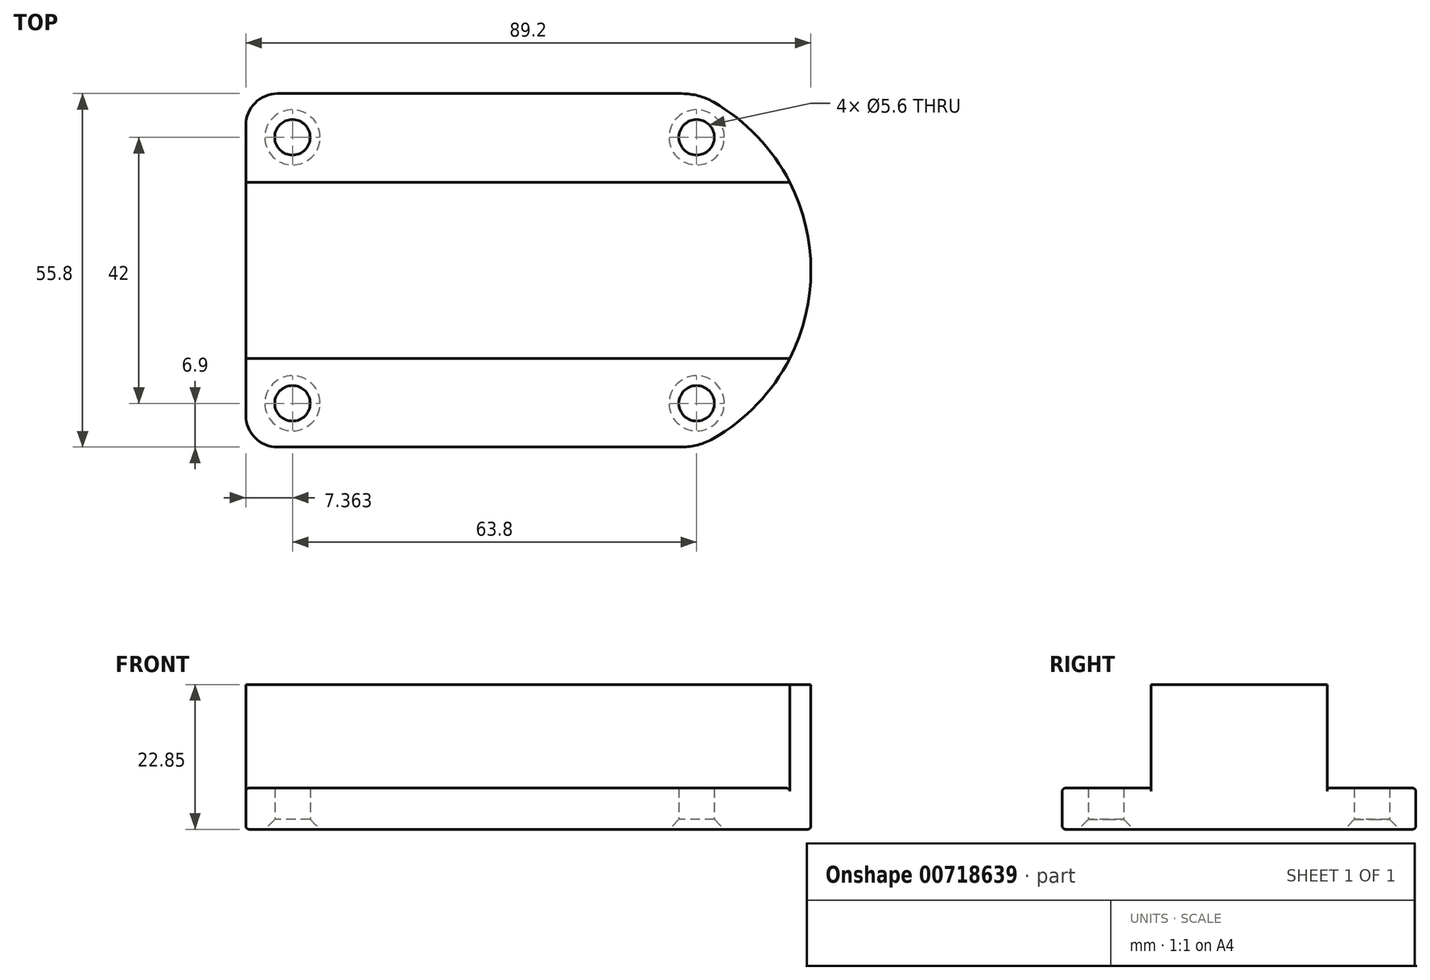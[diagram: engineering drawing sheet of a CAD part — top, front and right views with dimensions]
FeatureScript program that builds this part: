
annotation { "Feature Type Name" : "Feature", "Feature Type Description" : "" }
export const myFeature = defineFeature(function(context is Context, id is Id, definition is map)
    precondition{}
    {
        {
            var Q0;
            Q0=qCreatedBy(makeId("Top.planeOp"),FACE);
            var sketch = newSketch(context, id + "F0", { "sketchPlane" : qUnion([Q0])});
            skLineSegment(sketch, "E0.bottom", {"start": v(-38.88, -28.9) * mm, "end": v(-38.88, 16.9) * mm});
            skLineSegment(sketch, "E0.left", {"start": v(-33.88, -33.9) * mm, "end": v(29.94, -33.9) * mm});
            skLineSegment(sketch, "E0.right", {"start": v(-33.88, 21.9) * mm, "end": v(29.94, 21.9) * mm});
            skArc(sketch, "E1", {"start": v(34.9, -32.58) * mm, "mid": v(50.32, -6) * mm, "end": v(34.9, 20.58) * mm});
            skPoint(sketch, "E2.visualSharp", {"position": v(32.32, 21.9) * mm});
            skArc(sketch, "E2.filletArc", {"start": v(34.9, 20.58) * mm, "mid": v(32.51, 21.56) * mm, "end": v(29.94, 21.9) * mm});
            skPoint(sketch, "E3.visualSharp", {"position": v(32.32, -33.9) * mm});
            skArc(sketch, "E3.filletArc", {"start": v(29.94, -33.9) * mm, "mid": v(32.51, -33.56) * mm, "end": v(34.9, -32.58) * mm});
            skCircle(sketch, "E4", {"center": v(-31.52, 15) * mm, "radius": 2.8 * mm});
            skCircle(sketch, "E5", {"center": v(-31.52, -27) * mm, "radius": 2.8 * mm});
            skCircle(sketch, "E6", {"center": v(32.28, -27) * mm, "radius": 2.8 * mm});
            skCircle(sketch, "E7", {"center": v(32.28, 15) * mm, "radius": 2.8 * mm});
            skPoint(sketch, "E8.visualSharp", {"position": v(-38.88, 21.9) * mm});
            skArc(sketch, "E8.filletArc", {"start": v(-33.88, 21.9) * mm, "mid": v(-37.41, 20.44) * mm, "end": v(-38.88, 16.9) * mm});
            skPoint(sketch, "E9.visualSharp", {"position": v(-38.88, -33.9) * mm});
            skArc(sketch, "E9.filletArc", {"start": v(-38.88, -28.9) * mm, "mid": v(-37.41, -32.44) * mm, "end": v(-33.88, -33.9) * mm});
            skSolve(sketch);
        }
        {
            var Q0;
            Q0 = qSketchRegion(id + "F0", true);
            extrude(context, id + "F1", {"entities" : qUnion([Q0]), "depth" : 6.5 * mm, "offsetDistance" : 25 * mm});
        }
        {
            var Q0;
            Q0=makeQuery(id+"F1.opExtrude","CAP_FACE",FACE,{"disambiguationData":[OSD([sQuery(id+"F0.wireOp",EDGE,"E0.bottom"),sQuery(id+"F0.wireOp",EDGE,"E0.left"),sQuery(id+"F0.wireOp",EDGE,"E0.right"),sQuery(id+"F0.wireOp",EDGE,"E1"),sQuery(id+"F0.wireOp",EDGE,"E2.filletArc"),sQuery(id+"F0.wireOp",EDGE,"E3.filletArc"),sQuery(id+"F0.wireOp",EDGE,"E4"),sQuery(id+"F0.wireOp",EDGE,"E5"),sQuery(id+"F0.wireOp",EDGE,"E6"),sQuery(id+"F0.wireOp",EDGE,"E7")])],"isStart":false});
            var sketch = newSketch(context, id + "F2", { "sketchPlane" : qUnion([Q0])});
            skLineSegment(sketch, "E10", {"start": v(-38.88, -6) * mm, "end": v(-38.88, 7.9) * mm});
            skLineSegment(sketch, "E11", {"start": v(-38.88, -6) * mm, "end": v(-38.88, -19.9) * mm});
            skLineSegment(sketch, "E12.bottom", {"start": v(-38.88, 7.9) * mm, "end": v(46.99, 7.9) * mm});
            skLineSegment(sketch, "E12.top", {"start": v(-38.88, -19.9) * mm, "end": v(46.99, -19.9) * mm});
            skLineSegment(sketch, "E12.left", {"start": v(-38.88, 7.9) * mm, "end": v(-38.88, -19.9) * mm});
            skArc(sketch, "E13", {"start": v(46.99, -19.9) * mm, "mid": v(50.32, -6) * mm, "end": v(46.99, 7.9) * mm});
            skSolve(sketch);
        }
        {
            var Q0;
            Q0 = qSketchRegion(id + "F2", true);
            extrude(context, id + "F3", {"entities" : qUnion([Q0]), "operationType" : NewBodyOperationType.ADD, "depth" : 16.35 * mm, "offsetDistance" : 25 * mm});
        }
        {
            var Q0;
            Q0=makeQuery(id+"F1.opExtrude","CAP_EDGE",EDGE,{"disambiguationData":[OSD([sQuery(id+"F0.wireOp",EDGE,"E0.right")])],"isStart":true});
            var Q1;
            Q1=makeQuery(id+"F1.opExtrude","CAP_EDGE",EDGE,{"disambiguationData":[OSD([sQuery(id+"F0.wireOp",EDGE,"E8.filletArc")])],"isStart":true});
            var Q2;
            Q2=makeQuery(id+"F1.opExtrude","CAP_EDGE",EDGE,{"disambiguationData":[OSD([sQuery(id+"F0.wireOp",EDGE,"E0.right")])],"isStart":false});
            var Q3;
            Q3=makeQuery(id+"F1.opExtrude","CAP_EDGE",EDGE,{"disambiguationData":[OSD([sQuery(id+"F0.wireOp",EDGE,"E0.left")])],"isStart":false});
            var Q4;
            Q4=makeQuery(id+"F1.opExtrude","CAP_EDGE",EDGE,{"disambiguationData":[OSD([sQuery(id+"F0.wireOp",EDGE,"E0.left")])],"isStart":true});
            var Q5;
            Q5=makeQuery(id+"F1.opExtrude","CAP_EDGE",EDGE,{"disambiguationData":[OSD([sQuery(id+"F0.wireOp",EDGE,"E1")])],"isStart":true});
            var Q6;
            Q6=makeQuery(id+"F1.opExtrude","CAP_EDGE",EDGE,{"disambiguationData":[OSD([sQuery(id+"F0.wireOp",EDGE,"E0.bottom")])],"isStart":true});
            fillet(context, id + "F4", {"entities" : qUnion([Q0, Q1, Q2, Q3, Q4, Q5, Q6]), "radius" : 0.5 * mm, "tangentPropagation" : true, "allowEdgeOverflow" : false});
        }
        {
            var Q0;
            Q0=makeQuery(id+"F1.opExtrude","CAP_EDGE",EDGE,{"disambiguationData":[OSD([sQuery(id+"F0.wireOp",EDGE,"E4")])],"isStart":true});
            var Q1;
            Q1=makeQuery(id+"F1.opExtrude","CAP_EDGE",EDGE,{"disambiguationData":[OSD([sQuery(id+"F0.wireOp",EDGE,"E5")])],"isStart":true});
            var Q2;
            Q2=makeQuery(id+"F1.opExtrude","CAP_EDGE",EDGE,{"disambiguationData":[OSD([sQuery(id+"F0.wireOp",EDGE,"E6")])],"isStart":true});
            var Q3;
            Q3=makeQuery(id+"F1.opExtrude","CAP_EDGE",EDGE,{"disambiguationData":[OSD([sQuery(id+"F0.wireOp",EDGE,"E7")])],"isStart":true});
            chamfer(context, id + "F5", {"entities" : qUnion([Q0, Q1, Q2, Q3]), "width" : 1.56 * mm, "tangentPropagation" : true});
        }
    });
